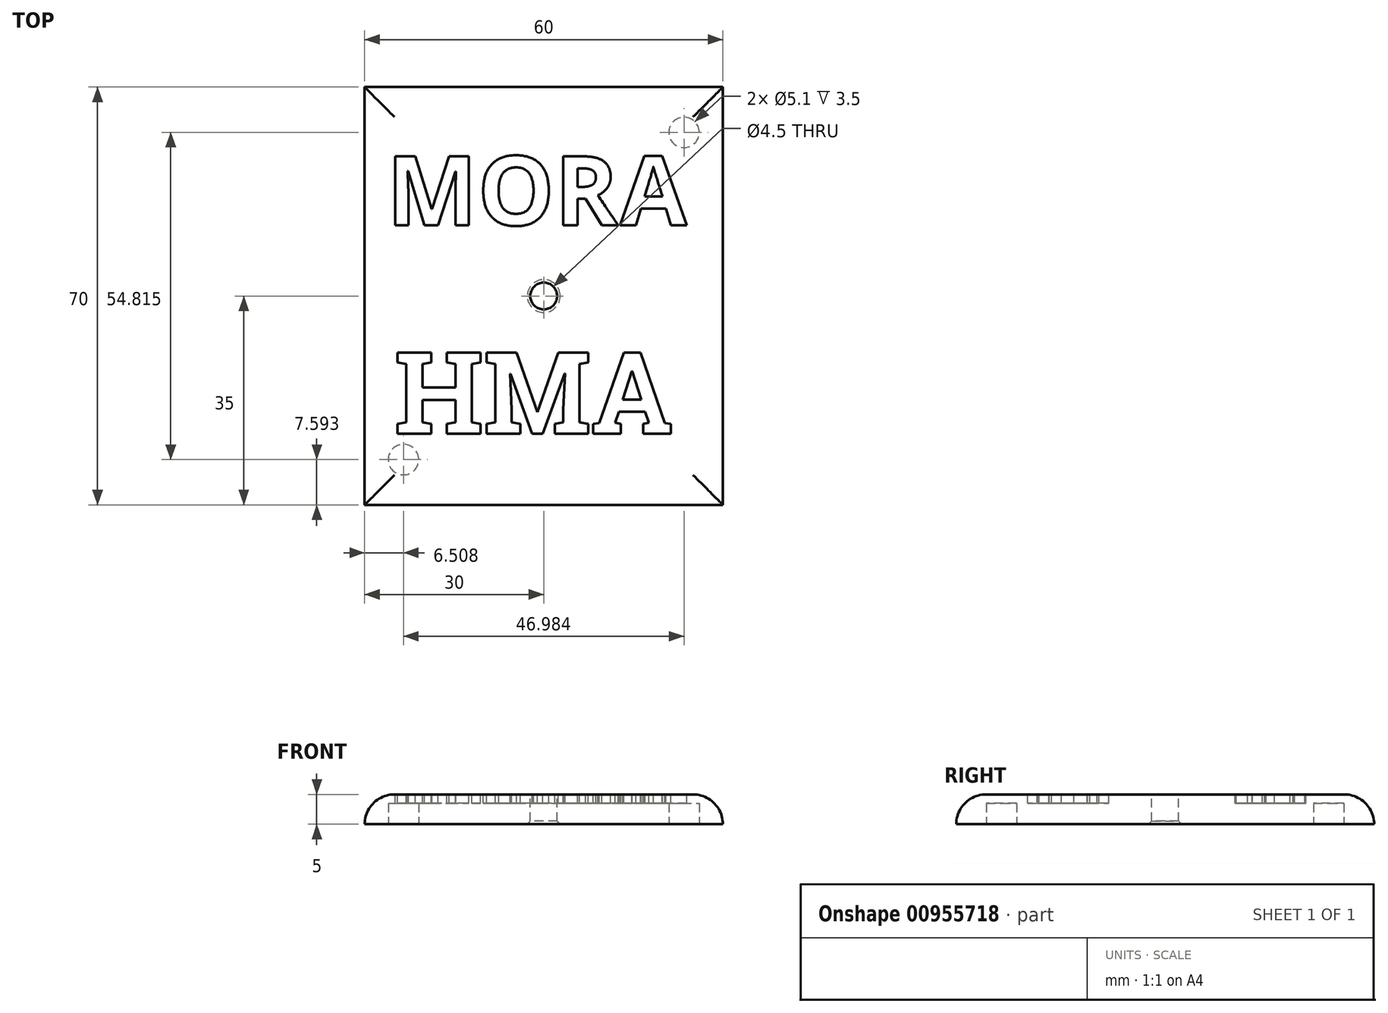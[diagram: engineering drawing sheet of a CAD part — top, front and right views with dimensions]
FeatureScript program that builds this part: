
annotation { "Feature Type Name" : "Feature", "Feature Type Description" : "" }
export const myFeature = defineFeature(function(context is Context, id is Id, definition is map)
    precondition{}
    {
        {
            var Q0;
            Q0=qCreatedBy(makeId("Top.planeOp"),FACE);
            var sketch = newSketch(context, id + "F0", { "sketchPlane" : qUnion([Q0])});
            skLineSegment(sketch, "E0.bottom", {"start": v(0, 0) * mm, "end": v(60, 0) * mm});
            skLineSegment(sketch, "E0.top", {"start": v(0, -70) * mm, "end": v(60, -70) * mm});
            skLineSegment(sketch, "E0.left", {"start": v(0, 0) * mm, "end": v(0, -70) * mm});
            skLineSegment(sketch, "E0.right", {"start": v(60, 0) * mm, "end": v(60, -70) * mm});
            skSolve(sketch);
        }
        {
            var Q0;
            Q0=makeQuery(id+"F0.imprint","IMPRINT",FACE,{"disambiguationData":[TD([[makeQuery(id+"F0.imprint","IMPRINT",EDGE,{"derivedFrom":sQuery(id+"F0.wireOp",EDGE,"E0.bottom")}),-1.0]])]});
            extrude(context, id + "F1", {"entities" : qUnion([Q0]), "depth" : 5 * mm, "offsetDistance" : 25 * mm});
        }
        {
            var Q0;
            Q0=makeQuery(id+"F1.opExtrude","CAP_FACE",FACE,{"disambiguationData":[OSD([sQuery(id+"F0.wireOp",EDGE,"E0.bottom"),sQuery(id+"F0.wireOp",EDGE,"E0.top"),sQuery(id+"F0.wireOp",EDGE,"E0.left"),sQuery(id+"F0.wireOp",EDGE,"E0.right")])],"isStart":false});
            var sketch = newSketch(context, id + "F2", { "sketchPlane" : qUnion([Q0])});
            skCircle(sketch, "E1", {"center": v(30, -35) * mm, "radius": 2.25 * mm});
            skPoint(sketch, "E2.trimOffspring.end.orphan", {"position": v(60, 0) * mm});
            skPoint(sketch, "E3.start.orphan", {"position": v(0, -70) * mm});
            skSolve(sketch);
        }
        {
            var Q0;
            Q0=makeQuery(id+"F2.imprint","IMPRINT",FACE,{"disambiguationData":[TD([[makeQuery(id+"F2.imprint","IMPRINT",EDGE,{"derivedFrom":sQuery(id+"F2.wireOp",EDGE,"E1")}),1.0]])]});
            extrude(context, id + "F3", {"entities" : qUnion([Q0]), "operationType" : NewBodyOperationType.REMOVE, "oppositeDirection" : true, "depth" : 25 * mm, "offsetDistance" : 25 * mm});
        }
        {
            var Q0;
            Q0=makeQuery(id+"F1.opExtrude","CAP_EDGE",EDGE,{"disambiguationData":[OSD([sQuery(id+"F0.wireOp",EDGE,"E0.top")])],"isStart":false});
            var Q1;
            Q1=makeQuery(id+"F1.opExtrude","CAP_EDGE",EDGE,{"disambiguationData":[OSD([sQuery(id+"F0.wireOp",EDGE,"E0.right")])],"isStart":false});
            var Q2;
            Q2=makeQuery(id+"F1.opExtrude","CAP_EDGE",EDGE,{"disambiguationData":[OSD([sQuery(id+"F0.wireOp",EDGE,"E0.bottom")])],"isStart":false});
            var Q3;
            Q3=makeQuery(id+"F1.opExtrude","CAP_EDGE",EDGE,{"disambiguationData":[OSD([sQuery(id+"F0.wireOp",EDGE,"E0.left")])],"isStart":false});
            fillet(context, id + "F4", {"entities" : qUnion([Q0, Q1, Q2, Q3]), "radius" : 5 * mm, "tangentPropagation" : true, "allowEdgeOverflow" : false});
        }
        {
            var Q0;
            Q0=makeQuery(id+"F1.opExtrude","CAP_FACE",FACE,{"disambiguationData":[OSD([sQuery(id+"F0.wireOp",EDGE,"E0.bottom"),sQuery(id+"F0.wireOp",EDGE,"E0.top"),sQuery(id+"F0.wireOp",EDGE,"E0.left"),sQuery(id+"F0.wireOp",EDGE,"E0.right")])],"isStart":true});
            var sketch = newSketch(context, id + "F5", { "sketchPlane" : qUnion([Q0])});
            skLineSegment(sketch, "E4", {"start": v(0, 70) * mm, "end": v(4.85, 64.34) * mm});
            skLineSegment(sketch, "E5", {"start": v(60, 0) * mm, "end": v(55.15, 5.66) * mm});
            skCircle(sketch, "E6", {"center": v(6.5, 62.4) * mm, "radius": 2.55 * mm});
            skCircle(sketch, "E7", {"center": v(53.5, 7.6) * mm, "radius": 2.55 * mm});
            skLineSegment(sketch, "E8.trimOffspring", {"start": v(55.15, 5.66) * mm, "end": v(60, 0) * mm});
            skSolve(sketch);
        }
        {
            var Q0;
            Q0=makeQuery(id+"F5.imprint","IMPRINT",FACE,{"disambiguationData":[TD([[makeQuery(id+"F5.imprint","IMPRINT",EDGE,{"derivedFrom":sQuery(id+"F5.wireOp",EDGE,"E7")}),1.0]])]});
            var Q1;
            Q1=makeQuery(id+"F5.imprint","IMPRINT",FACE,{"disambiguationData":[TD([[makeQuery(id+"F5.imprint","IMPRINT",EDGE,{"derivedFrom":sQuery(id+"F5.wireOp",EDGE,"E6")}),1.0]])]});
            extrude(context, id + "F6", {"entities" : qUnion([Q0, Q1]), "operationType" : NewBodyOperationType.REMOVE, "oppositeDirection" : true, "depth" : 3.5 * mm, "offsetDistance" : 25 * mm});
        }
        {
            var Q0;
            Q0=makeQuery(id+"F6.boolean.opBoolean","COPY",EDGE,{"derivedFrom":makeQuery(id+"F6.opExtrude","CAP_EDGE",EDGE,{"disambiguationData":[OSD([sQuery(id+"F5.wireOp",EDGE,"E6")])],"isStart":true})});
            var Q1;
            Q1=makeQuery(id+"F6.boolean.opBoolean","COPY",EDGE,{"derivedFrom":makeQuery(id+"F6.opExtrude","CAP_EDGE",EDGE,{"disambiguationData":[OSD([sQuery(id+"F5.wireOp",EDGE,"E7")])],"isStart":true})});
            var Q2;
            Q2=makeQuery(id+"F3.boolean.opBoolean","INTERSECT",EDGE,{"derivedFrom":[makeQuery(id+"F1.opExtrude","CAP_FACE",FACE,{"disambiguationData":[OSD([sQuery(id+"F0.wireOp",EDGE,"E0.bottom"),sQuery(id+"F0.wireOp",EDGE,"E0.top"),sQuery(id+"F0.wireOp",EDGE,"E0.left"),sQuery(id+"F0.wireOp",EDGE,"E0.right")])],"isStart":true}),makeQuery(id+"F3.opExtrude","SWEPT_FACE",FACE,{"disambiguationData":[OSD([sQuery(id+"F2.wireOp",EDGE,"E1")])]})]});
            chamfer(context, id + "F7", {"entities" : qUnion([Q0, Q1, Q2]), "width" : 0.5 * mm, "tangentPropagation" : true});
        }
        {
            var Q0;
            Q0=makeQuery(id+"F1.opExtrude","CAP_FACE",FACE,{"disambiguationData":[OSD([sQuery(id+"F0.wireOp",EDGE,"E0.bottom"),sQuery(id+"F0.wireOp",EDGE,"E0.top"),sQuery(id+"F0.wireOp",EDGE,"E0.left"),sQuery(id+"F0.wireOp",EDGE,"E0.right")])],"isStart":false});
            var sketch = newSketch(context, id + "F8", { "sketchPlane" : qUnion([Q0])});
            skText(sketch, "E9", { "text": "MORA", "fontName": "OpenSans-Bold.ttf"});
            const initialGuessF8  = {"E9": [0.0037, -0.02313, 1, 0, 0.01163]};
            skSetInitialGuess(sketch, initialGuessF8);
            skSolve(sketch);
        }
        {
            var Q0;
            Q0 = qSketchRegion(id + "F8", true);
            extrude(context, id + "F9", {"entities" : qUnion([Q0]), "operationType" : NewBodyOperationType.REMOVE, "oppositeDirection" : true, "depth" : 1.5 * mm, "offsetDistance" : 25 * mm});
        }
        {
            var Q0;
            {var subQ0=sQuery(id+"F0.wireOp",EDGE,"E0.bottom");var subQ1=sQuery(id+"F0.wireOp",EDGE,"E0.right");var subQ2=sQuery(id+"F0.wireOp",EDGE,"E0.left");var subQ3=sQuery(id+"F0.wireOp",EDGE,"E0.top");Q0=makeQuery(id+"F9.boolean.opBoolean","SPLIT",FACE,{"disambiguationData":[TD([makeQuery(id+"F3.boolean.opBoolean","COPY",FACE,{"derivedFrom":makeQuery(id+"F3.opExtrude","SWEPT_FACE",FACE,{"disambiguationData":[OSD([sQuery(id+"F2.wireOp",EDGE,"E1")])]})})])],"derivedFrom":makeQuery(id+"F1.opExtrude","CAP_FACE",FACE,{"disambiguationData":[OSD([subQ0,subQ3,subQ2,subQ1])],"isStart":false})});}
            var sketch = newSketch(context, id + "F10", { "sketchPlane" : qUnion([Q0])});
            skText(sketch, "E10", { "text": "HMA", "fontName": "RobotoSlab-Bold.ttf"});
            const initialGuessF10  = {"E10": [0.005, -0.05805, 1, 0, 0.01375]};
            skSetInitialGuess(sketch, initialGuessF10);
            skSolve(sketch);
        }
        {
            var Q0;
            Q0=makeQuery(id+"F10.imprint","IMPRINT",FACE,{"disambiguationData":[TD([[makeQuery(id+"F10.imprint","IMPRINT",EDGE,{"derivedFrom":sQuery(id+"F10.wireOp",EDGE,"E10.sketch_text.stroke-0")}),-1.0]])]});
            var Q1;
            Q1=makeQuery(id+"F10.imprint","IMPRINT",FACE,{"disambiguationData":[TD([[makeQuery(id+"F10.imprint","IMPRINT",EDGE,{"derivedFrom":sQuery(id+"F10.wireOp",EDGE,"E10.sketch_text.stroke-30")}),-1.0]])]});
            var Q2;
            Q2=makeQuery(id+"F10.imprint","IMPRINT",FACE,{"disambiguationData":[TD([[makeQuery(id+"F10.imprint","IMPRINT",EDGE,{"derivedFrom":sQuery(id+"F10.wireOp",EDGE,"E10.sketch_text.stroke-61")}),-1.0]])]});
            extrude(context, id + "F11", {"entities" : qUnion([Q0, Q1, Q2]), "operationType" : NewBodyOperationType.REMOVE, "oppositeDirection" : true, "depth" : 1.5 * mm, "offsetDistance" : 25 * mm});
        }
    });
